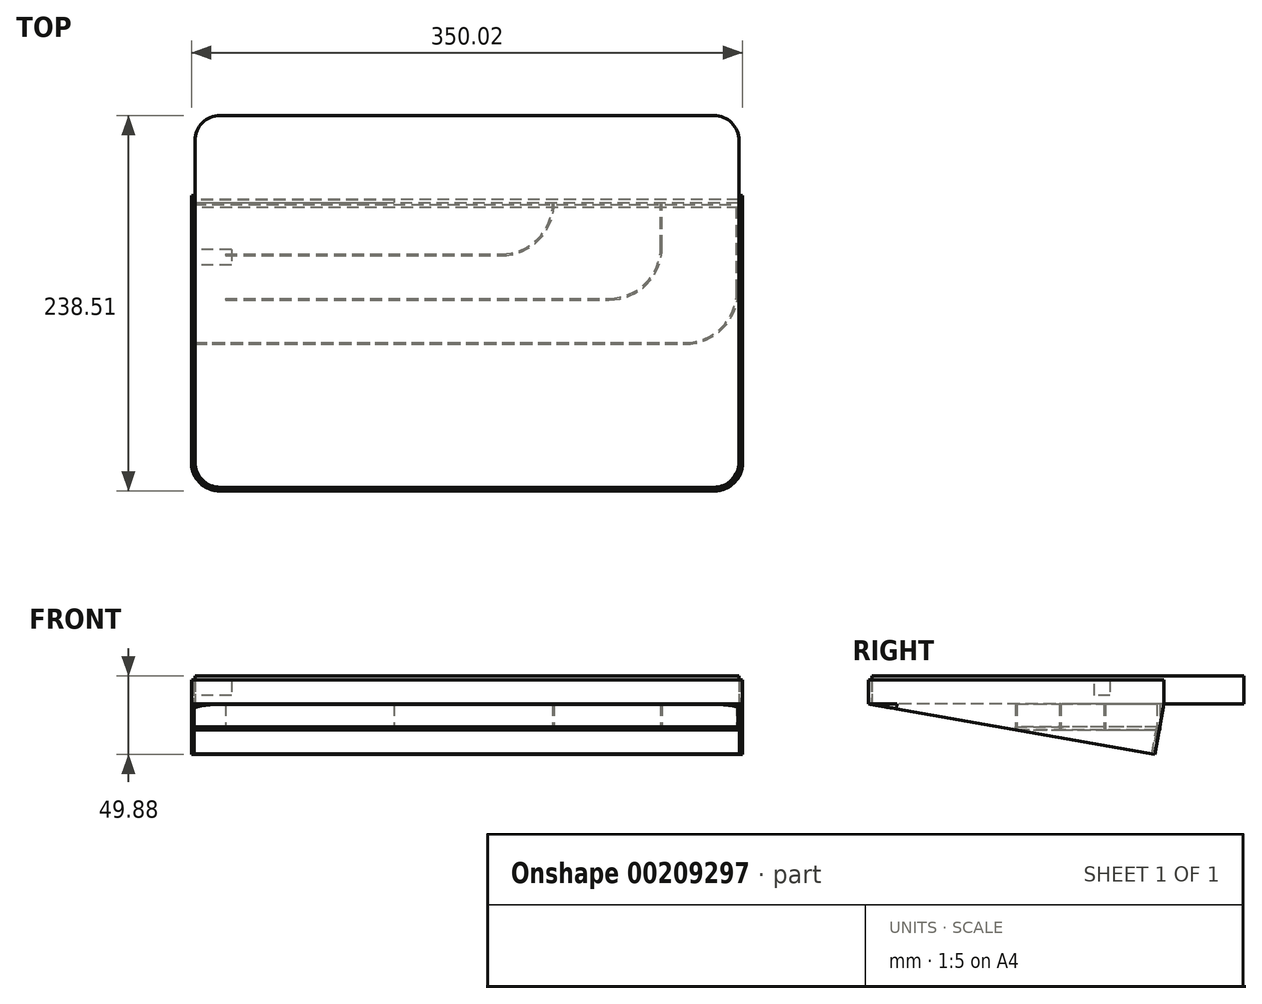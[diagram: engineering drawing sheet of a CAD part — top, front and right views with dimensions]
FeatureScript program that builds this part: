
annotation { "Feature Type Name" : "Feature", "Feature Type Description" : "" }
export const myFeature = defineFeature(function(context is Context, id is Id, definition is map)
    precondition{}
    {
        {
            var Q0;
            Q0=qCreatedBy(makeId("Top.planeOp"),FACE);
            var sketch = newSketch(context, id + "F0", { "sketchPlane" : qUnion([Q0])});
            skLineSegment(sketch, "E0.bottom", {"start": v(156.84, 118.11) * mm, "end": v(-156.84, 118.11) * mm});
            skLineSegment(sketch, "E0.top", {"start": v(156.84, -118.11) * mm, "end": v(-156.84, -118.11) * mm});
            skLineSegment(sketch, "E0.left", {"start": v(172.72, 102.24) * mm, "end": v(172.72, -102.24) * mm});
            skLineSegment(sketch, "E0.right", {"start": v(-172.72, 102.24) * mm, "end": v(-172.72, -102.24) * mm});
            skPoint(sketch, "E0.middle", {"position": v(0, 0) * mm});
            skPoint(sketch, "E1.visualSharp", {"position": v(-172.72, -118.11) * mm});
            skArc(sketch, "E1.filletArc", {"start": v(-172.72, -102.24) * mm, "mid": v(-168.07, -113.46) * mm, "end": v(-156.84, -118.11) * mm});
            skPoint(sketch, "E2.visualSharp", {"position": v(172.72, -118.11) * mm});
            skArc(sketch, "E2.filletArc", {"start": v(156.84, -118.11) * mm, "mid": v(168.07, -113.46) * mm, "end": v(172.72, -102.24) * mm});
            skPoint(sketch, "E3.visualSharp", {"position": v(172.72, 118.11) * mm});
            skArc(sketch, "E3.filletArc", {"start": v(172.72, 102.24) * mm, "mid": v(168.07, 113.46) * mm, "end": v(156.84, 118.11) * mm});
            skPoint(sketch, "E4.visualSharp", {"position": v(-172.72, 118.11) * mm});
            skArc(sketch, "E4.filletArc", {"start": v(-156.84, 118.11) * mm, "mid": v(-168.07, 113.46) * mm, "end": v(-172.72, 102.24) * mm});
            skArc(sketch, "E5.0", {"start": v(173.23, 102.24) * mm, "mid": v(168.43, 113.82) * mm, "end": v(156.84, 118.62) * mm});
            skLineSegment(sketch, "E5.1", {"start": v(173.23, 102.24) * mm, "end": v(173.23, -102.24) * mm});
            skLineSegment(sketch, "E5.2", {"start": v(156.84, 118.62) * mm, "end": v(-156.84, 118.62) * mm});
            skArc(sketch, "E5.3", {"start": v(156.84, -118.62) * mm, "mid": v(168.43, -113.82) * mm, "end": v(173.23, -102.24) * mm});
            skArc(sketch, "E5.4", {"start": v(-156.84, 118.62) * mm, "mid": v(-168.43, 113.82) * mm, "end": v(-173.23, 102.24) * mm});
            skLineSegment(sketch, "E5.5", {"start": v(-173.23, 102.24) * mm, "end": v(-173.23, -102.24) * mm});
            skArc(sketch, "E5.6", {"start": v(-173.23, -102.24) * mm, "mid": v(-168.43, -113.82) * mm, "end": v(-156.84, -118.62) * mm});
            skLineSegment(sketch, "E5.7", {"start": v(156.84, -118.62) * mm, "end": v(-156.84, -118.62) * mm});
            skArc(sketch, "E6.0", {"start": v(175, 102.24) * mm, "mid": v(169.69, 115.08) * mm, "end": v(156.84, 120.4) * mm});
            skLineSegment(sketch, "E6.1", {"start": v(175, 102.24) * mm, "end": v(175, -102.24) * mm});
            skLineSegment(sketch, "E6.2", {"start": v(156.84, 120.4) * mm, "end": v(-156.84, 120.4) * mm});
            skArc(sketch, "E6.3", {"start": v(156.84, -120.4) * mm, "mid": v(169.69, -115.08) * mm, "end": v(175, -102.24) * mm});
            skArc(sketch, "E6.4", {"start": v(-156.84, 120.4) * mm, "mid": v(-169.69, 115.08) * mm, "end": v(-175, 102.24) * mm});
            skLineSegment(sketch, "E6.5", {"start": v(-175, 102.24) * mm, "end": v(-175, -102.24) * mm});
            skArc(sketch, "E6.6", {"start": v(-175, -102.24) * mm, "mid": v(-169.69, -115.08) * mm, "end": v(-156.84, -120.4) * mm});
            skLineSegment(sketch, "E6.7", {"start": v(156.84, -120.4) * mm, "end": v(-156.84, -120.4) * mm});
            skLineSegment(sketch, "E7", {"start": v(-175, 67.31) * mm, "end": v(175, 67.3) * mm});
            skSolve(sketch);
        }
        {
            var Q0;
            Q0=makeQuery(id+"F0.imprint","IMPRINT",FACE,{"disambiguationData":[TD([[makeQuery(id+"F0.imprint","IMPRINT",EDGE,{"derivedFrom":sQuery(id+"F0.wireOp",EDGE,"E0.bottom")}),1.0]])]});
            var Q1;
            Q1=makeQuery(id+"F0.imprint","IMPRINT",FACE,{"disambiguationData":[TD([[makeQuery(id+"F0.imprint","IMPRINT",EDGE,{"derivedFrom":sQuery(id+"F0.wireOp",EDGE,"E0.top")}),-1.0]])]});
            extrude(context, id + "F1", {"entities" : qUnion([Q0, Q1]), "depth" : 17.78 * mm});
        }
        {
            var Q0;
            {var subQ10=sQuery(id+"F0.wireOp",EDGE,"E5.3");Q0=makeQuery(id+"F0.imprint","IMPRINT",FACE,{"disambiguationData":[TD([[makeQuery(id+"F0.imprint","IMPRINT",EDGE,{"derivedFrom":subQ10}),-1.0]])]});}
            extrude(context, id + "F2", {"entities" : qUnion([Q0]), "depth" : 15.24 * mm});
        }
        {
            var Q0;
            Q0=sQuery(id+"F0.wireOp",EDGE,"E6.7");
            cPlane(context, id + "F3", {"entities" : qUnion([Q0]), "cplaneType" : CPlaneType.LINE_ANGLE, "offset" : 25.4 * mm, "angle" : 100 * degree, "width" : 152.4 * mm, "height" : 152.4 * mm});
        }
        {
            var Q0;
            Q0=qCreatedBy(id+"F3.planeOp",FACE);
            var sketch = newSketch(context, id + "F4", { "sketchPlane" : qUnion([Q0])});
            skLineSegment(sketch, "E8.0.0", {"start": v(173.23, 66.29) * mm, "end": v(175, 66.29) * mm});
            skLineSegment(sketch, "E8.0.1", {"start": v(175, 66.29) * mm, "end": v(175, -100.68) * mm});
            skEllipticalArc(sketch, "E8.0.2", {});
            skLineSegment(sketch, "E8.0.3", {"start": v(156.84, -118.57) * mm, "end": v(-156.84, -118.57) * mm});
            skEllipticalArc(sketch, "E8.0.4", {});
            skLineSegment(sketch, "E8.0.5", {"start": v(-175, -100.68) * mm, "end": v(-175, 66.29) * mm});
            skLineSegment(sketch, "E8.0.6", {"start": v(-175, 66.29) * mm, "end": v(-173.23, 66.29) * mm});
            skLineSegment(sketch, "E8.0.7", {"start": v(-173.23, 66.29) * mm, "end": v(-173.23, -100.68) * mm});
            skEllipticalArc(sketch, "E8.0.8", {});
            skLineSegment(sketch, "E8.0.9", {"start": v(-156.84, -116.82) * mm, "end": v(156.84, -116.82) * mm});
            skEllipticalArc(sketch, "E8.0.10", {});
            skLineSegment(sketch, "E8.0.11", {"start": v(173.23, -100.68) * mm, "end": v(173.23, 66.29) * mm});
            const initialGuessF4  = {"E8.0.2": [0.156845, -0.1006818206292031, 1, 0, 0.018161, 0.017885093602454705, 4.71238898038469, 0], "E8.0.4": [-0.156845, -0.1006818206292031, 1, 0, 0.018161, 0.017885093602454705, 3.141592653589793, 4.71238898038469], "E8.0.8": [-0.156845, -0.1006818206292031, -1, 0, 0.016383, 0.016134105417599, 0, 1.5707963267948966], "E8.0.10": [0.156845, -0.1006818206292031, -1, 0, 0.016383, 0.016134105417599, 1.5707963267948966, 3.141592653589793]};
            skSetInitialGuess(sketch, initialGuessF4);
            skSolve(sketch);
        }
        {
            var Q1;
            Q1=makeQuery(id+"F4.imprint","IMPRINT",FACE,{"disambiguationData":[TD([[makeQuery(id+"F4.imprint","IMPRINT",EDGE,{"derivedFrom":sQuery(id+"F4.wireOp",EDGE,"E8.0.0")}),-1.0]])]});
            var Q2;
            Q2=makeQuery(id+"F2.opExtrude","CAP_FACE",FACE,{"disambiguationData":[OSD([sQuery(id+"F0.wireOp",EDGE,"E5.1"),sQuery(id+"F0.wireOp",EDGE,"E5.3"),sQuery(id+"F0.wireOp",EDGE,"E5.5"),sQuery(id+"F0.wireOp",EDGE,"E5.6"),sQuery(id+"F0.wireOp",EDGE,"E5.7"),sQuery(id+"F0.wireOp",EDGE,"E6.1"),sQuery(id+"F0.wireOp",EDGE,"E6.3"),sQuery(id+"F0.wireOp",EDGE,"E6.5"),sQuery(id+"F0.wireOp",EDGE,"E6.6"),sQuery(id+"F0.wireOp",EDGE,"E6.7"),sQuery(id+"F0.wireOp",EDGE,"E7")])],"isStart":true});
            loft(context, id + "F5", {"operationType" : NewBodyOperationType.ADD, "sheetProfilesArray" : [{ "sheetProfileEntities" : qUnion([Q1]) }, { "sheetProfileEntities" : qUnion([Q2]) }]});
        }
        {
            var Q0;
            {var subQ0=sQuery(id+"F0.wireOp",EDGE,"E6.5");Q0=makeQuery(id+"F5.boolean.opBoolean","MERGE",FACE,{"derivedFrom":[makeQuery(id+"F2.opExtrude","SWEPT_FACE",FACE,{"disambiguationData":[OSD([subQ0])]}),makeQuery(id+"F5.opLoft","SWEPT_FACE",FACE,{"disambiguationData":[OSD([subQ0,sQuery(id+"F0.wireOp",EDGE,"E6.6"),sQuery(id+"F0.wireOp",EDGE,"E7"),sQuery(id+"F4.wireOp",EDGE,"E8.0.4"),sQuery(id+"F4.wireOp",EDGE,"E8.0.5"),sQuery(id+"F4.wireOp",EDGE,"E8.0.6")])]})]});}
            var sketch = newSketch(context, id + "F6", { "sketchPlane" : qUnion([Q0])});
            skLineSegment(sketch, "E9.0", {"start": v(-118.11, 17.78) * mm, "end": v(-118.11, 0) * mm});
            skLineSegment(sketch, "E10.0", {"start": v(-67.31, 15.24) * mm, "end": v(102.24, 15.24) * mm});
            skLineSegment(sketch, "E11.0", {"start": v(-61.65, -32.1) * mm, "end": v(-67.31, 0) * mm});
            skLineSegment(sketch, "E11.1", {"start": v(-67.31, 15.24) * mm, "end": v(-67.31, 0) * mm});
            skLineSegment(sketch, "E11.2", {"start": v(-61.65, -32.1) * mm, "end": v(102.78, -3.1) * mm});
            skLineSegment(sketch, "E12.0", {"start": v(120.4, 15.24) * mm, "end": v(120.4, 0) * mm});
            skLineSegment(sketch, "E12.1", {"start": v(102.24, 15.24) * mm, "end": v(120.4, 15.24) * mm});
            skLineSegment(sketch, "E13", {"start": v(120.4, 0) * mm, "end": v(102.78, -3.1) * mm});
            skLineSegment(sketch, "E14", {"start": v(-33.02, 15.24) * mm, "end": v(-33.02, 5.33) * mm});
            skLineSegment(sketch, "E15", {"start": v(-33.02, 5.33) * mm, "end": v(-23.11, 5.33) * mm});
            skLineSegment(sketch, "E16", {"start": v(-23.11, 5.33) * mm, "end": v(-23.11, 15.24) * mm});
            skLineSegment(sketch, "E17", {"start": v(-67.31, 0) * mm, "end": v(120.4, 0) * mm});
            skLineSegment(sketch, "E18.bottom", {"start": v(-57.15, 0) * mm, "end": v(27.18, 0) * mm});
            skLineSegment(sketch, "E18.top", {"start": v(-57.15, -14.48) * mm, "end": v(27.18, -14.48) * mm});
            skLineSegment(sketch, "E18.left", {"start": v(-57.15, 0) * mm, "end": v(-57.15, -14.48) * mm});
            skLineSegment(sketch, "E18.right", {"start": v(27.18, 0) * mm, "end": v(27.18, -14.48) * mm});
            skLineSegment(sketch, "E19", {"start": v(-59.65, -31.75) * mm, "end": v(-65.25, 0) * mm});
            skLineSegment(sketch, "E20", {"start": v(-57.15, -14.48) * mm, "end": v(-64.76, -14.48) * mm});
            skSolve(sketch);
        }
        {
            var Q0;
            {var subQ0=sQuery(id+"F6.wireOp",EDGE,"E11.2");var subQ1=sQuery(id+"F6.wireOp",EDGE,"E11.0");var subQ2=makeQuery(id+"F6.imprint","INTERSECT",VERTEX,{"derivedFrom":[subQ1,subQ0]});Q0=makeQuery(id+"F6.imprint","IMPRINT",FACE,{"disambiguationData":[TD([[makeQuery(id+"F6.imprint","IMPRINT",EDGE,{"disambiguationData":[TD([[subQ2,-1.0]])],"derivedFrom":subQ1}),-1.0]])]});}
            var Q1;
            {var subQ0=sQuery(id+"F0.wireOp",EDGE,"E5.1");Q1=makeQuery(id+"F5.boolean.opBoolean","MERGE",FACE,{"derivedFrom":[makeQuery(id+"F2.opExtrude","SWEPT_FACE",FACE,{"disambiguationData":[OSD([subQ0])]}),makeQuery(id+"F5.opLoft","SWEPT_FACE",FACE,{"disambiguationData":[OSD([subQ0,sQuery(id+"F0.wireOp",EDGE,"E5.3"),sQuery(id+"F0.wireOp",EDGE,"E7"),sQuery(id+"F4.wireOp",EDGE,"E8.0.0"),sQuery(id+"F4.wireOp",EDGE,"E8.0.10"),sQuery(id+"F4.wireOp",EDGE,"E8.0.11")])]})]});}
            extrude(context, id + "F7", {"entities" : qUnion([Q0]), "operationType" : NewBodyOperationType.ADD, "endBound" : BoundingType.UP_TO_SURFACE, "oppositeDirection" : true, "endBoundEntityFace" : qUnion([Q1]), "depth" : 25.4 * mm});
        }
        {
            var Q0;
            Q0=makeQuery(id+"F6.imprint","IMPRINT",FACE,{"disambiguationData":[TD([[makeQuery(id+"F6.imprint","IMPRINT",EDGE,{"derivedFrom":sQuery(id+"F6.wireOp",EDGE,"E18.bottom")}),-1.0]])]});
            var Q1;
            {var subQ0=sQuery(id+"F6.wireOp",EDGE,"E14");Q1=makeQuery(id+"F6.imprint","IMPRINT",FACE,{"disambiguationData":[TD([[makeQuery(id+"F6.imprint","IMPRINT",EDGE,{"derivedFrom":subQ0}),1.0]])]});}
            extrude(context, id + "F8", {"entities" : qUnion([Q0, Q1]), "operationType" : NewBodyOperationType.REMOVE, "oppositeDirection" : true, "depth" : 25.4 * mm});
        }
        {
            var Q0;
            Q0=qCreatedBy(makeId("Top.planeOp"),FACE);
            cPlane(context, id + "F9", {"entities" : qUnion([Q0]), "cplaneType" : CPlaneType.OFFSET, "offset" : 14.48 * mm, "oppositeDirection" : true, "width" : 152.4 * mm, "height" : 152.4 * mm});
        }
        {
            var Q0;
            Q0=qCreatedBy(id+"F9.planeOp",FACE);
            var sketch = newSketch(context, id + "F10", { "sketchPlane" : qUnion([Q0])});
            skLineSegment(sketch, "E21.0", {"start": v(-173.23, -27.18) * mm, "end": v(-173.23, -102.24) * mm});
            skLineSegment(sketch, "E22", {"start": v(-173.23, 62.7) * mm, "end": v(-173.23, 57.15) * mm});
            skPoint(sketch, "E23.0.start.orphan", {"position": v(-173.23, -27.18) * mm});
            skLineSegment(sketch, "E24", {"start": v(-173.23, -27.18) * mm, "end": v(138.56, -27.18) * mm});
            skPoint(sketch, "E25.endSnap0", {"position": v(-0.5, -27.18) * mm});
            skLineSegment(sketch, "E26", {"start": v(-173.23, 57.15) * mm, "end": v(-173.23, 30.06) * mm});
            skLineSegment(sketch, "E27", {"start": v(-173.23, 62.7) * mm, "end": v(-46.23, 62.7) * mm});
            skLineSegment(sketch, "E28", {"start": v(-173.23, 29.04) * mm, "end": v(-173.23, 1.95) * mm});
            skLineSegment(sketch, "E29", {"start": v(-173.23, 0.93) * mm, "end": v(-173.23, -26.16) * mm});
            skLineSegment(sketch, "E30", {"start": v(123.95, 34.59) * mm, "end": v(123.95, 62.7) * mm});
            skLineSegment(sketch, "E31", {"start": v(55.37, 62.7) * mm, "end": v(55.37, 62.7) * mm});
            skLineSegment(sketch, "E32", {"start": v(172.21, 62.7) * mm, "end": v(172.21, 6.48) * mm});
            skPoint(sketch, "E33.visualSharp", {"position": v(55.37, 29.04) * mm});
            skArc(sketch, "E33.filletArc", {"start": v(21.72, 29.04) * mm, "mid": v(45.51, 38.9) * mm, "end": v(55.37, 62.7) * mm});
            skPoint(sketch, "E34.visualSharp", {"position": v(123.95, 0.93) * mm});
            skArc(sketch, "E34.filletArc", {"start": v(90.3, 0.93) * mm, "mid": v(114.1, 10.79) * mm, "end": v(123.95, 34.59) * mm});
            skPoint(sketch, "E35.visualSharp", {"position": v(172.21, -27.18) * mm});
            skArc(sketch, "E35.filletArc", {"start": v(138.56, -27.18) * mm, "mid": v(162.35, -17.32) * mm, "end": v(172.21, 6.48) * mm});
            skLineSegment(sketch, "E36", {"start": v(54.36, 62.7) * mm, "end": v(54.36, 62.7) * mm});
            skLineSegment(sketch, "E37", {"start": v(-173.23, 1.95) * mm, "end": v(-173.23, 1.95) * mm});
            skLineSegment(sketch, "E38", {"start": v(122.94, 34.59) * mm, "end": v(122.94, 62.7) * mm});
            skLineSegment(sketch, "E39", {"start": v(-173.23, -26.16) * mm, "end": v(138.56, -26.16) * mm});
            skLineSegment(sketch, "E40", {"start": v(171.2, 6.48) * mm, "end": v(171.2, 62.7) * mm});
            skLineSegment(sketch, "E41", {"start": v(-173.23, 30.06) * mm, "end": v(-173.23, 29.04) * mm});
            skLineSegment(sketch, "E42", {"start": v(-173.23, -26.16) * mm, "end": v(-173.23, -27.18) * mm});
            skLineSegment(sketch, "E43", {"start": v(-173.23, 1.95) * mm, "end": v(-173.23, 0.93) * mm});
            skLineSegment(sketch, "E44", {"start": v(54.36, 62.7) * mm, "end": v(55.37, 62.7) * mm});
            skLineSegment(sketch, "E45", {"start": v(55.37, 62.7) * mm, "end": v(122.94, 62.7) * mm});
            skLineSegment(sketch, "E46", {"start": v(122.94, 62.7) * mm, "end": v(123.95, 62.7) * mm});
            skLineSegment(sketch, "E47", {"start": v(123.95, 62.7) * mm, "end": v(171.2, 62.7) * mm});
            skLineSegment(sketch, "E48", {"start": v(171.2, 62.7) * mm, "end": v(172.21, 62.7) * mm});
            skPoint(sketch, "E49.visualSharp", {"position": v(54.36, 30.06) * mm});
            skArc(sketch, "E49.filletArc", {"start": v(21.72, 30.06) * mm, "mid": v(44.8, 39.62) * mm, "end": v(54.36, 62.7) * mm});
            skPoint(sketch, "E50.visualSharp", {"position": v(122.94, 1.95) * mm});
            skArc(sketch, "E50.filletArc", {"start": v(90.3, 1.95) * mm, "mid": v(113.38, 11.5) * mm, "end": v(122.94, 34.59) * mm});
            skPoint(sketch, "E51.visualSharp", {"position": v(171.2, -26.16) * mm});
            skArc(sketch, "E51.filletArc", {"start": v(138.56, -26.16) * mm, "mid": v(161.64, -16.6) * mm, "end": v(171.2, 6.48) * mm});
            skLineSegment(sketch, "E52.0", {"start": v(173.23, 64.76) * mm, "end": v(-46.23, 64.76) * mm});
            skLineSegment(sketch, "E53", {"start": v(-46.23, 64.76) * mm, "end": v(-46.23, 62.7) * mm});
            skLineSegment(sketch, "E54", {"start": v(-46.23, 62.7) * mm, "end": v(54.36, 62.7) * mm});
            skLineSegment(sketch, "E55", {"start": v(-46.23, 64.76) * mm, "end": v(-173.23, 64.76) * mm});
            skLineSegment(sketch, "E56", {"start": v(-173.23, 64.76) * mm, "end": v(-173.23, 62.7) * mm});
            skLineSegment(sketch, "E57", {"start": v(-153.42, 30.06) * mm, "end": v(-153.42, 1.95) * mm});
            skLineSegment(sketch, "E58", {"start": v(-153.42, 29.04) * mm, "end": v(21.72, 29.04) * mm});
            skLineSegment(sketch, "E59", {"start": v(-153.42, 30.06) * mm, "end": v(21.72, 30.06) * mm});
            skLineSegment(sketch, "E60", {"start": v(-153.42, 0.93) * mm, "end": v(-153.42, 0.93) * mm});
            skLineSegment(sketch, "E61", {"start": v(-153.42, 1.95) * mm, "end": v(-153.42, 0.93) * mm});
            skLineSegment(sketch, "E62", {"start": v(-153.42, 1.95) * mm, "end": v(90.3, 1.95) * mm});
            skLineSegment(sketch, "E63", {"start": v(-153.42, 0.93) * mm, "end": v(90.3, 0.93) * mm});
            skSolve(sketch);
        }
        {
            var Q0;
            Q0 = qSketchRegion(id + "F10", true);
            extrude(context, id + "F11", {"entities" : qUnion([Q0]), "operationType" : NewBodyOperationType.ADD, "oppositeDirection" : true, "depth" : 1.9 * mm});
        }
        {
            var Q0;
            Q0=makeQuery(id+"F10.imprint","IMPRINT",FACE,{"disambiguationData":[TD([[makeQuery(id+"F10.imprint","IMPRINT",EDGE,{"derivedFrom":sQuery(id+"F10.wireOp",EDGE,"E27")}),1.0]])]});
            var Q1;
            {var subQ1=sQuery(id+"F10.wireOp",EDGE,"E44");Q1=makeQuery(id+"F10.imprint","IMPRINT",FACE,{"disambiguationData":[TD([[makeQuery(id+"F10.imprint","IMPRINT",EDGE,{"derivedFrom":subQ1}),-1.0]])]});}
            var Q2;
            Q2=makeQuery(id+"F10.imprint","IMPRINT",FACE,{"disambiguationData":[TD([[makeQuery(id+"F10.imprint","IMPRINT",EDGE,{"derivedFrom":sQuery(id+"F10.wireOp",EDGE,"E30")}),1.0]])]});
            var Q3;
            Q3=makeQuery(id+"F10.imprint","IMPRINT",FACE,{"disambiguationData":[TD([[makeQuery(id+"F10.imprint","IMPRINT",EDGE,{"derivedFrom":sQuery(id+"F10.wireOp",EDGE,"E24")}),1.0]])]});
            extrude(context, id + "F12", {"entities" : qUnion([Q0, Q1, Q2, Q3]), "depth" : 14.35 * mm, "hasSecondDirection" : true, "secondDirectionOppositeDirection" : true, "secondDirectionDepth" : 2.03 * mm});
        }
    });
